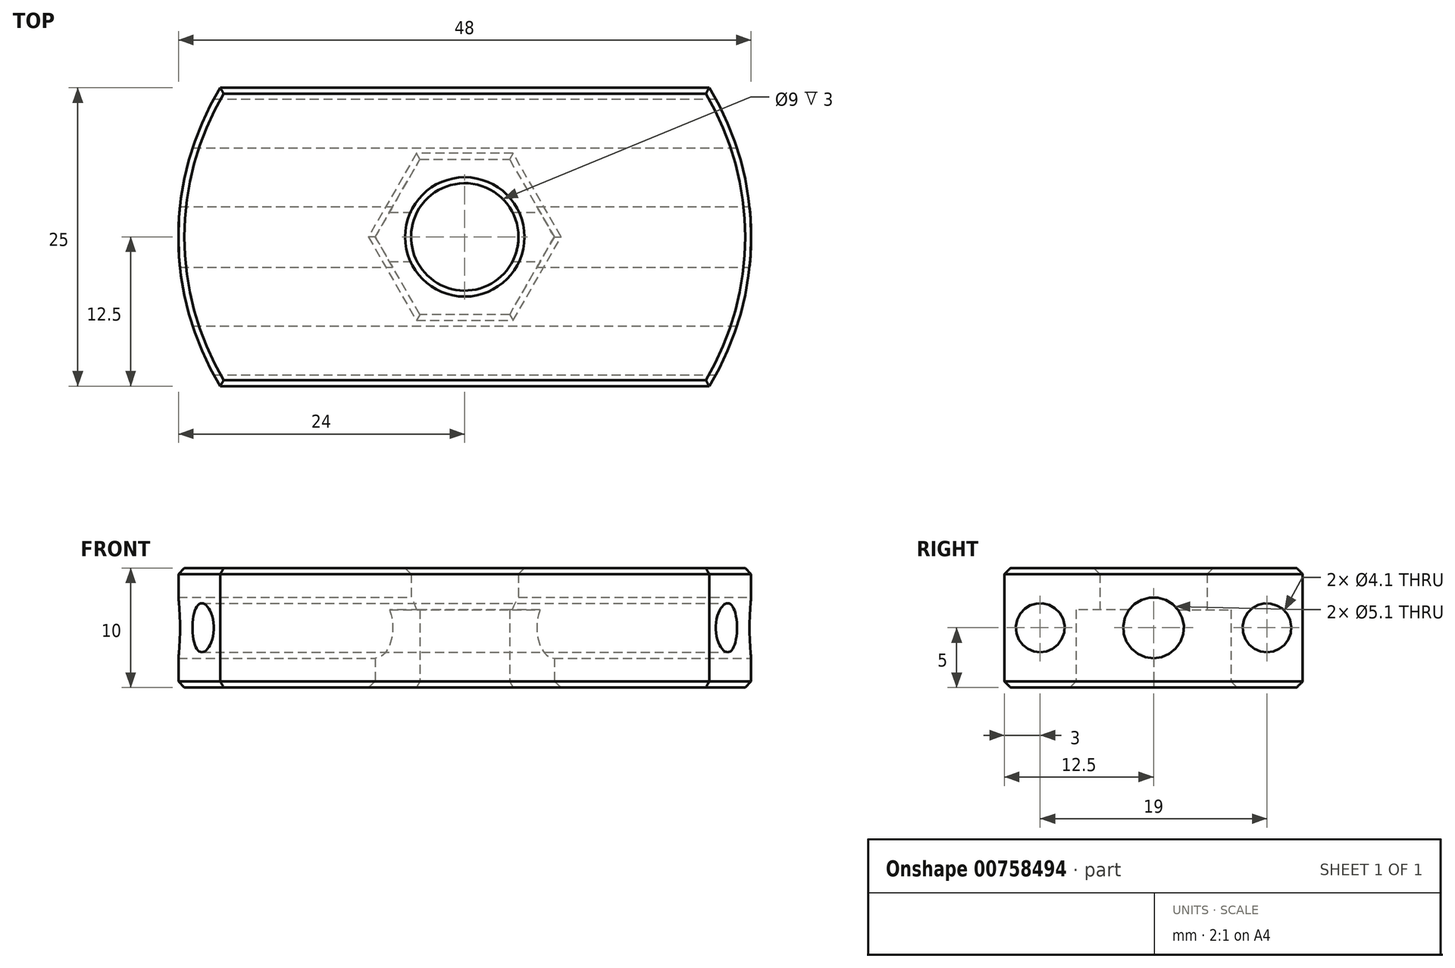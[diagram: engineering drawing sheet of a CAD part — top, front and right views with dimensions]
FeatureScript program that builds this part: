
annotation { "Feature Type Name" : "Feature", "Feature Type Description" : "" }
export const myFeature = defineFeature(function(context is Context, id is Id, definition is map)
    precondition{}
    {
        {
            var Q0;
            Q0=qCreatedBy(makeId("Top.planeOp"),FACE);
            var sketch = newSketch(context, id + "F0", { "sketchPlane" : qUnion([Q0])});
            skCircle(sketch, "E0.cCircle", {"center": v(0, 0) * mm, "radius": 6.5 * mm, "construction": true});
            skLineSegment(sketch, "E0.0", {"start": v(-3.75, 6.5) * mm, "end": v(3.75, 6.5) * mm});
            skLineSegment(sketch, "E0.1", {"start": v(3.75, 6.5) * mm, "end": v(7.5, 0) * mm});
            skLineSegment(sketch, "E0.2", {"start": v(7.5, 0) * mm, "end": v(3.75, -6.5) * mm});
            skLineSegment(sketch, "E0.3", {"start": v(3.75, -6.5) * mm, "end": v(-3.75, -6.5) * mm});
            skLineSegment(sketch, "E0.4", {"start": v(-3.75, -6.5) * mm, "end": v(-7.5, 0) * mm});
            skLineSegment(sketch, "E0.5", {"start": v(-7.5, 0) * mm, "end": v(-3.75, 6.5) * mm});
            skPoint(sketch, "E0.0.midPoint", {"position": v(0, 6.5) * mm});
            skCircle(sketch, "E1", {"center": v(0, 0) * mm, "radius": 15 * mm});
            skCircle(sketch, "E2", {"center": v(0, 0) * mm, "radius": 24 * mm});
            skCircle(sketch, "E3", {"center": v(0, 0) * mm, "radius": 4.5 * mm});
            skLineSegment(sketch, "E4.bottom", {"start": v(20.49, 12.5) * mm, "end": v(-20.49, 12.5) * mm});
            skLineSegment(sketch, "E4.top", {"start": v(20.49, -12.5) * mm, "end": v(-20.49, -12.5) * mm});
            skLineSegment(sketch, "E4.left", {"start": v(20.49, 12.5) * mm, "end": v(20.49, -12.5) * mm});
            skLineSegment(sketch, "E4.right", {"start": v(-20.49, 12.5) * mm, "end": v(-20.49, -12.5) * mm});
            skSolve(sketch);
        }
        {
            var Q0;
            {var subQ0=sQuery(id+"F0.wireOp",EDGE,"E4.right");Q0=makeQuery(id+"F0.imprint","IMPRINT",FACE,{"disambiguationData":[TD([[makeQuery(id+"F0.imprint","IMPRINT",EDGE,{"derivedFrom":subQ0}),-1.0]])]});}
            var Q1;
            {var subQ5=sQuery(id+"F0.wireOp",EDGE,"E4.right");Q1=makeQuery(id+"F0.imprint","IMPRINT",FACE,{"disambiguationData":[TD([[makeQuery(id+"F0.imprint","IMPRINT",EDGE,{"derivedFrom":subQ5}),1.0]])]});}
            var Q2;
            Q2=makeQuery(id+"F0.imprint","IMPRINT",FACE,{"disambiguationData":[TD([[makeQuery(id+"F0.imprint","IMPRINT",EDGE,{"derivedFrom":sQuery(id+"F0.wireOp",EDGE,"E0.0")}),1.0]])]});
            var Q3;
            {var subQ0=sQuery(id+"F0.wireOp",EDGE,"E4.bottom");var subQ1=sQuery(id+"F0.wireOp",EDGE,"E1");var subQ2=makeQuery(id+"F0.imprint","INTERSECT",VERTEX,{"disambiguationData":[OD(0.0)],"derivedFrom":[subQ1,subQ0]});Q3=makeQuery(id+"F0.imprint","IMPRINT",FACE,{"disambiguationData":[TD([[makeQuery(id+"F0.imprint","IMPRINT",EDGE,{"disambiguationData":[TD([[subQ2,1.0]])],"derivedFrom":subQ1}),1.0]])]});}
            var Q4;
            {var subQ5=sQuery(id+"F0.wireOp",EDGE,"E4.left");Q4=makeQuery(id+"F0.imprint","IMPRINT",FACE,{"disambiguationData":[TD([[makeQuery(id+"F0.imprint","IMPRINT",EDGE,{"derivedFrom":subQ5}),-1.0]])]});}
            var Q5;
            {var subQ0=sQuery(id+"F0.wireOp",EDGE,"E4.left");Q5=makeQuery(id+"F0.imprint","IMPRINT",FACE,{"disambiguationData":[TD([[makeQuery(id+"F0.imprint","IMPRINT",EDGE,{"derivedFrom":subQ0}),1.0]])]});}
            var Q6;
            {var subQ0=sQuery(id+"F0.wireOp",EDGE,"E4.top");var subQ1=sQuery(id+"F0.wireOp",EDGE,"E1");var subQ2=makeQuery(id+"F0.imprint","INTERSECT",VERTEX,{"disambiguationData":[OD(0.0)],"derivedFrom":[subQ1,subQ0]});Q6=makeQuery(id+"F0.imprint","IMPRINT",FACE,{"disambiguationData":[TD([[makeQuery(id+"F0.imprint","IMPRINT",EDGE,{"disambiguationData":[TD([[subQ2,-1.0]])],"derivedFrom":subQ1}),1.0]])]});}
            var Q7;
            Q7=makeQuery(id+"F0.imprint","IMPRINT",FACE,{"disambiguationData":[TD([[makeQuery(id+"F0.imprint","IMPRINT",EDGE,{"derivedFrom":sQuery(id+"F0.wireOp",EDGE,"E0.0")}),-1.0]])]});
            extrude(context, id + "F1", {"entities" : qUnion([Q0, Q1, Q2, Q3, Q4, Q5, Q6, Q7]), "depth" : 10 * mm, "offsetDistance" : 25 * mm});
        }
        {
            var Q0;
            Q0=makeQuery(id+"F0.imprint","IMPRINT",FACE,{"disambiguationData":[TD([[makeQuery(id+"F0.imprint","IMPRINT",EDGE,{"derivedFrom":sQuery(id+"F0.wireOp",EDGE,"E0.0")}),-1.0]])]});
            extrude(context, id + "F2", {"entities" : qUnion([Q0]), "operationType" : NewBodyOperationType.REMOVE, "depth" : 6.5 * mm, "offsetDistance" : 25 * mm});
        }
        {
            var Q0;
            Q0=qCreatedBy(makeId("Right.planeOp"),FACE);
            cPlane(context, id + "F3", {"entities" : qUnion([Q0]), "cplaneType" : CPlaneType.OFFSET, "offset" : 60 * mm, "width" : 150 * mm, "height" : 150 * mm});
        }
        {
            var Q0;
            Q0=qCreatedBy(id+"F3.planeOp",FACE);
            var sketch = newSketch(context, id + "F4", { "sketchPlane" : qUnion([Q0])});
            skPoint(sketch, "E5", {"position": v(9.5, 5) * mm});
            skPoint(sketch, "E6", {"position": v(0, 5) * mm});
            skPoint(sketch, "E7.MirrorP", {"position": v(-9.5, 5) * mm});
            skSolve(sketch);
        }
        {
            var Q0;
            Q0=sQuery(id+"F4.wireOp",VERTEX,"E7.MirrorP");
            var Q1;
            Q1=sQuery(id+"F4.wireOp",VERTEX,"E5");
            var Q2;
            Q2=makeQuery(id+"F1.opExtrude","SWEPT_BODY",BODY,{"disambiguationData":[OSD([sQuery(id+"F0.wireOp",EDGE,"E1"),sQuery(id+"F0.wireOp",EDGE,"E2"),sQuery(id+"F0.wireOp",EDGE,"E3"),sQuery(id+"F0.wireOp",EDGE,"E4.bottom"),sQuery(id+"F0.wireOp",EDGE,"E4.top")])]});
            hole(context, id + "F5", {"style" : HoleStyle.SIMPLE, "endStyle" : HoleEndStyle.THROUGH, "holeDiameter" : 4.1 * mm, "majorDiameter" : 5 * mm, "isTappedThrough" : true, "tappedDepth" : 12 * mm, "tapClearance" : 3, "locations" : qUnion([Q0, Q1]), "scope" : qUnion([Q2])});
        }
        {
            var Q0;
            Q0=sQuery(id+"F4.wireOp",VERTEX,"E6");
            var Q1;
            Q1=makeQuery(id+"F1.opExtrude","SWEPT_BODY",BODY,{"disambiguationData":[OSD([sQuery(id+"F0.wireOp",EDGE,"E1"),sQuery(id+"F0.wireOp",EDGE,"E2"),sQuery(id+"F0.wireOp",EDGE,"E3"),sQuery(id+"F0.wireOp",EDGE,"E4.bottom"),sQuery(id+"F0.wireOp",EDGE,"E4.top")])]});
            hole(context, id + "F6", {"style" : HoleStyle.SIMPLE, "endStyle" : HoleEndStyle.THROUGH, "holeDiameter" : 5.1 * mm, "majorDiameter" : 5 * mm, "isTappedThrough" : true, "tappedDepth" : 12 * mm, "tapClearance" : 3, "locations" : qUnion([Q0]), "scope" : qUnion([Q1])});
        }
        {
            var Q0;
            Q0=makeQuery(id+"F1.opExtrude","CAP_FACE",FACE,{"disambiguationData":[OSD([sQuery(id+"F0.wireOp",EDGE,"E1"),sQuery(id+"F0.wireOp",EDGE,"E2"),sQuery(id+"F0.wireOp",EDGE,"E3"),sQuery(id+"F0.wireOp",EDGE,"E4.bottom"),sQuery(id+"F0.wireOp",EDGE,"E4.top")])],"isStart":true});
            var Q1;
            Q1=makeQuery(id+"F1.opExtrude","CAP_FACE",FACE,{"disambiguationData":[OSD([sQuery(id+"F0.wireOp",EDGE,"E1"),sQuery(id+"F0.wireOp",EDGE,"E2"),sQuery(id+"F0.wireOp",EDGE,"E3"),sQuery(id+"F0.wireOp",EDGE,"E4.bottom"),sQuery(id+"F0.wireOp",EDGE,"E4.top")])],"isStart":false});
            chamfer(context, id + "F7", {"entities" : qUnion([Q0, Q1]), "width" : 0.5 * mm, "tangentPropagation" : true});
        }
    });
